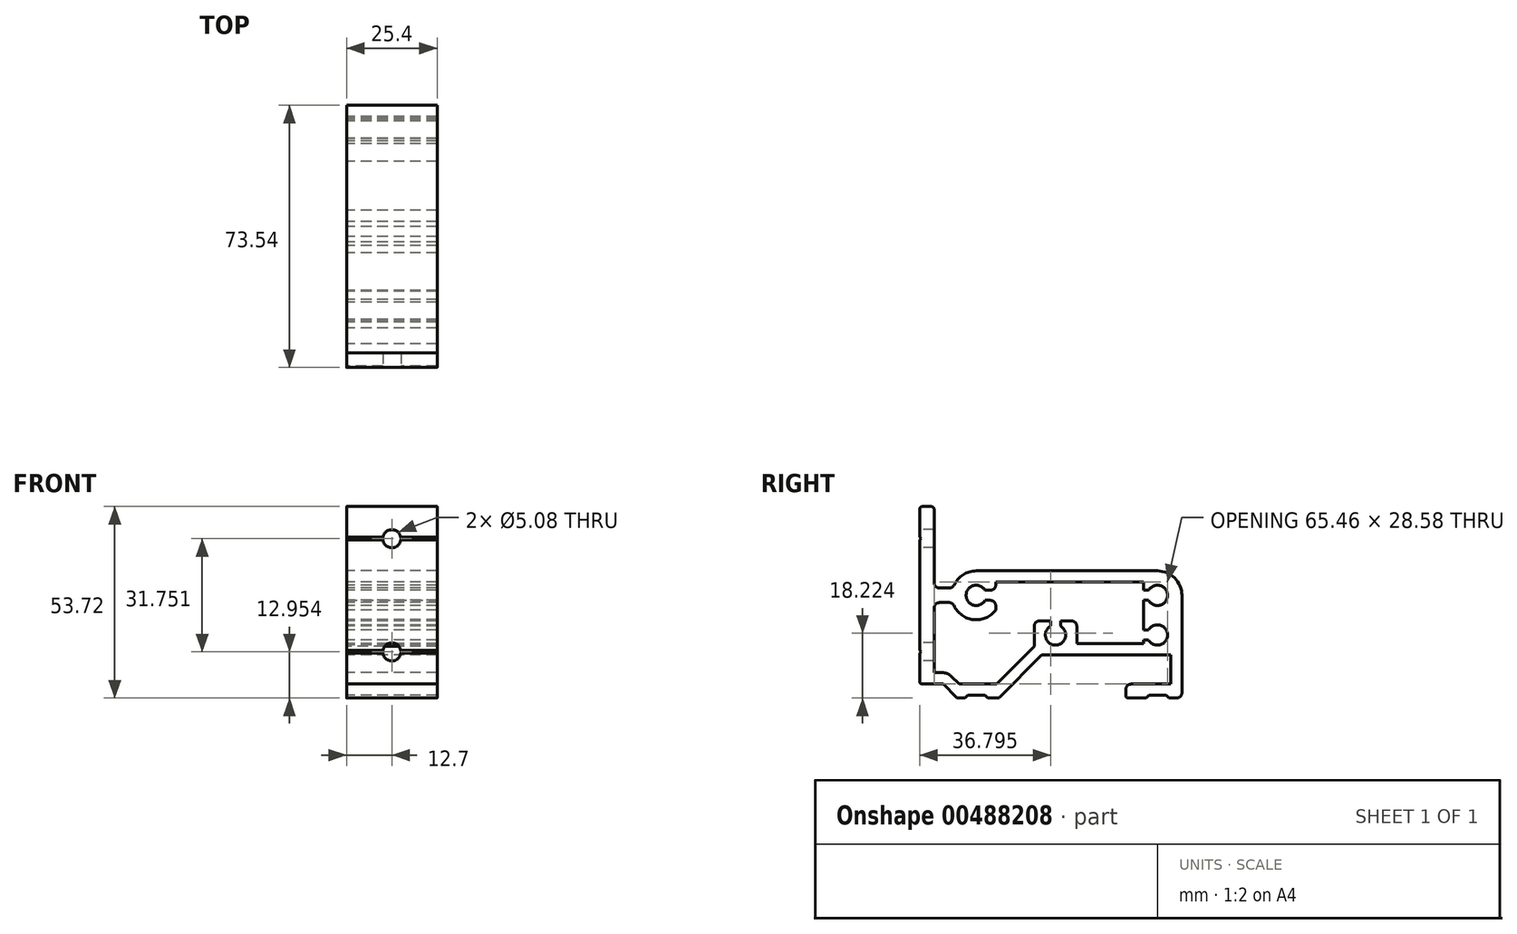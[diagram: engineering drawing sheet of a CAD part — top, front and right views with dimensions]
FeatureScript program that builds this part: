
annotation { "Feature Type Name" : "Feature", "Feature Type Description" : "" }
export const myFeature = defineFeature(function(context is Context, id is Id, definition is map)
    precondition{}
    {
        {
            var Q0;
            Q0=qCreatedBy(makeId("Right.planeOp"),FACE);
            var sketch = newSketch(context, id + "F0", { "sketchPlane" : qUnion([Q0])});
            skLineSegment(sketch, "E0", {"start": v(-16.95, 3.37) * mm, "end": v(-18.41, 3.37) * mm});
            skArc(sketch, "E1", {"start": v(-18.41, 3.37) * mm, "mid": v(-23.74, 1.97) * mm, "end": v(-18.41, 0.57) * mm});
            skLineSegment(sketch, "E2", {"start": v(-18.41, 0.57) * mm, "end": v(-16.95, 0.57) * mm});
            skArc(sketch, "E3", {"start": v(-16.95, 0.57) * mm, "mid": v(-15.88, 0.13) * mm, "end": v(-15.43, -0.95) * mm});
            skLineSegment(sketch, "E4", {"start": v(-15.43, -0.95) * mm, "end": v(-15.43, -2.18) * mm});
            skArc(sketch, "E5", {"start": v(-15.43, -2.18) * mm, "mid": v(-21.62, -4.85) * mm, "end": v(-27.1, -0.94) * mm});
            skArc(sketch, "E6", {"start": v(-27.1, -0.94) * mm, "mid": v(-27.66, -0.3) * mm, "end": v(-28.48, -0.06) * mm});
            skLineSegment(sketch, "E7", {"start": v(-28.48, -0.06) * mm, "end": v(-31.18, -0.06) * mm});
            skArc(sketch, "E8", {"start": v(-31.18, -0.06) * mm, "mid": v(-32.26, -0.5) * mm, "end": v(-32.7, -1.59) * mm});
            skLineSegment(sketch, "E9", {"start": v(-32.7, -1.59) * mm, "end": v(-32.7, -19.75) * mm});
            skLineSegment(sketch, "E10", {"start": v(-32.7, -19.75) * mm, "end": v(-30.16, -19.75) * mm});
            skArc(sketch, "E11", {"start": v(-30.16, -19.75) * mm, "mid": v(-28.95, -20) * mm, "end": v(-27.92, -20.68) * mm});
            skLineSegment(sketch, "E12", {"start": v(-27.92, -20.68) * mm, "end": v(-25.67, -22.92) * mm});
            skLineSegment(sketch, "E13", {"start": v(-25.67, -22.92) * mm, "end": v(-15.18, -22.92) * mm});
            skLineSegment(sketch, "E14", {"start": v(-15.18, -22.92) * mm, "end": v(-4.64, -12.38) * mm});
            skLineSegment(sketch, "E15", {"start": v(-4.64, -12.38) * mm, "end": v(-4.64, -6.73) * mm});
            skArc(sketch, "E16", {"start": v(-4.64, -6.73) * mm, "mid": v(-4.19, -5.65) * mm, "end": v(-3.11, -5.2) * mm});
            skLineSegment(sketch, "E17", {"start": v(-3.11, -5.2) * mm, "end": v(-0.06, -5.2) * mm});
            skLineSegment(sketch, "E18", {"start": v(-0.06, -5.2) * mm, "end": v(-0.06, -6.67) * mm});
            skArc(sketch, "E19", {"start": v(-0.06, -6.67) * mm, "mid": v(1.33, -11.99) * mm, "end": v(2.73, -6.67) * mm});
            skLineSegment(sketch, "E20", {"start": v(2.73, -6.67) * mm, "end": v(2.73, -5.2) * mm});
            skLineSegment(sketch, "E21", {"start": v(2.73, -5.2) * mm, "end": v(5.78, -5.2) * mm});
            skArc(sketch, "E22", {"start": v(5.78, -5.2) * mm, "mid": v(6.86, -5.65) * mm, "end": v(7.3, -6.73) * mm});
            skLineSegment(sketch, "E23", {"start": v(7.3, -6.73) * mm, "end": v(7.3, -11.62) * mm});
            skLineSegment(sketch, "E24", {"start": v(7.3, -11.62) * mm, "end": v(25.97, -11.62) * mm});
            skLineSegment(sketch, "E25", {"start": v(25.97, -11.62) * mm, "end": v(25.97, -10.54) * mm});
            skLineSegment(sketch, "E26", {"start": v(25.97, -10.54) * mm, "end": v(27.43, -10.54) * mm});
            skArc(sketch, "E27", {"start": v(27.43, -10.54) * mm, "mid": v(32.75, -9.14) * mm, "end": v(27.43, -7.75) * mm});
            skLineSegment(sketch, "E28", {"start": v(27.43, -7.75) * mm, "end": v(25.97, -7.75) * mm});
            skLineSegment(sketch, "E29", {"start": v(25.97, -7.75) * mm, "end": v(25.97, 0.57) * mm});
            skLineSegment(sketch, "E30", {"start": v(25.97, 0.57) * mm, "end": v(27.43, 0.57) * mm});
            skArc(sketch, "E31", {"start": v(27.43, 0.57) * mm, "mid": v(32.75, 1.97) * mm, "end": v(27.43, 3.37) * mm});
            skLineSegment(sketch, "E32", {"start": v(27.43, 3.37) * mm, "end": v(25.97, 3.37) * mm});
            skLineSegment(sketch, "E33", {"start": v(25.97, 3.37) * mm, "end": v(25.97, 5.65) * mm});
            skLineSegment(sketch, "E34", {"start": v(25.97, 5.65) * mm, "end": v(-15.43, 5.65) * mm});
            skLineSegment(sketch, "E35", {"start": v(-15.43, 5.65) * mm, "end": v(-15.43, 4.89) * mm});
            skArc(sketch, "E36", {"start": v(-15.43, 4.89) * mm, "mid": v(-15.88, 3.81) * mm, "end": v(-16.95, 3.37) * mm});
            skLineSegment(sketch, "E37", {"start": v(-36.77, 18.22) * mm, "end": v(-36.77, 26.1) * mm});
            skArc(sketch, "E38", {"start": v(-36.77, 26.1) * mm, "mid": v(-36.54, 26.64) * mm, "end": v(-36, 26.86) * mm});
            skLineSegment(sketch, "E39", {"start": v(-36, 26.86) * mm, "end": v(-33.46, 26.86) * mm});
            skArc(sketch, "E40", {"start": v(-33.46, 26.86) * mm, "mid": v(-32.93, 26.64) * mm, "end": v(-32.7, 26.1) * mm});
            skLineSegment(sketch, "E41", {"start": v(-32.7, 26.1) * mm, "end": v(-32.7, 5.52) * mm});
            skArc(sketch, "E42", {"start": v(-32.7, 5.52) * mm, "mid": v(-32.26, 4.45) * mm, "end": v(-31.18, 4) * mm});
            skLineSegment(sketch, "E43", {"start": v(-31.18, 4) * mm, "end": v(-28.48, 4) * mm});
            skArc(sketch, "E44", {"start": v(-28.48, 4) * mm, "mid": v(-27.66, 4.24) * mm, "end": v(-27.1, 4.88) * mm});
            skArc(sketch, "E45", {"start": v(-27.1, 4.88) * mm, "mid": v(-24.57, 7.76) * mm, "end": v(-20.9, 8.83) * mm});
            skLineSegment(sketch, "E46", {"start": v(-20.9, 8.83) * mm, "end": v(29.9, 8.83) * mm});
            skArc(sketch, "E47", {"start": v(29.9, 8.83) * mm, "mid": v(34.76, 6.82) * mm, "end": v(36.77, 1.97) * mm});
            skLineSegment(sketch, "E48", {"start": v(36.77, 1.97) * mm, "end": v(36.77, -25.34) * mm});
            skArc(sketch, "E49", {"start": v(36.77, -25.34) * mm, "mid": v(36.32, -26.41) * mm, "end": v(35.24, -26.86) * mm});
            skLineSegment(sketch, "E50", {"start": v(35.24, -26.86) * mm, "end": v(33.08, -26.86) * mm});
            skLineSegment(sketch, "E51", {"start": v(33.08, -26.86) * mm, "end": v(32.32, -26.1) * mm});
            skLineSegment(sketch, "E52", {"start": v(32.32, -26.1) * mm, "end": v(27.5, -26.1) * mm});
            skLineSegment(sketch, "E53", {"start": v(27.5, -26.1) * mm, "end": v(26.73, -26.86) * mm});
            skLineSegment(sketch, "E54", {"start": v(26.73, -26.86) * mm, "end": v(21.78, -26.86) * mm});
            skArc(sketch, "E55", {"start": v(21.78, -26.86) * mm, "mid": v(21.24, -26.64) * mm, "end": v(21.02, -26.1) * mm});
            skLineSegment(sketch, "E56", {"start": v(21.02, -26.1) * mm, "end": v(21.02, -24.45) * mm});
            skArc(sketch, "E57", {"start": v(21.02, -24.45) * mm, "mid": v(21.46, -23.37) * mm, "end": v(22.54, -22.92) * mm});
            skLineSegment(sketch, "E58", {"start": v(22.54, -22.92) * mm, "end": v(33.6, -22.92) * mm});
            skLineSegment(sketch, "E59", {"start": v(33.6, -22.92) * mm, "end": v(33.6, -14.8) * mm});
            skLineSegment(sketch, "E60", {"start": v(33.6, -14.8) * mm, "end": v(-2.56, -14.8) * mm});
            skLineSegment(sketch, "E61", {"start": v(-2.56, -14.8) * mm, "end": v(-14.4, -26.64) * mm});
            skArc(sketch, "E62", {"start": v(-14.4, -26.64) * mm, "mid": v(-14.65, -26.8) * mm, "end": v(-14.94, -26.86) * mm});
            skLineSegment(sketch, "E63", {"start": v(-14.94, -26.86) * mm, "end": v(-17.72, -26.86) * mm});
            skLineSegment(sketch, "E64", {"start": v(-17.72, -26.86) * mm, "end": v(-18.48, -26.1) * mm});
            skLineSegment(sketch, "E65", {"start": v(-18.48, -26.1) * mm, "end": v(-23.3, -26.1) * mm});
            skLineSegment(sketch, "E66", {"start": v(-23.3, -26.1) * mm, "end": v(-24.07, -26.86) * mm});
            skLineSegment(sketch, "E67", {"start": v(-24.07, -26.86) * mm, "end": v(-25.9, -26.86) * mm});
            skArc(sketch, "E68", {"start": v(-25.9, -26.86) * mm, "mid": v(-26.2, -26.8) * mm, "end": v(-26.45, -26.64) * mm});
            skLineSegment(sketch, "E69", {"start": v(-26.45, -26.64) * mm, "end": v(-30.16, -22.92) * mm});
            skLineSegment(sketch, "E70", {"start": v(-30.16, -22.92) * mm, "end": v(-36, -22.92) * mm});
            skArc(sketch, "E71", {"start": v(-36, -22.92) * mm, "mid": v(-36.54, -22.7) * mm, "end": v(-36.77, -22.16) * mm});
            skLineSegment(sketch, "E72", {"start": v(-36.77, -22.16) * mm, "end": v(-36.77, -14.29) * mm});
            skLineSegment(sketch, "E73", {"start": v(-36.77, -14.29) * mm, "end": v(-36.39, -13.9) * mm});
            skLineSegment(sketch, "E74", {"start": v(-36.39, -13.9) * mm, "end": v(-36.77, -13.53) * mm});
            skLineSegment(sketch, "E75", {"start": v(-36.77, -13.53) * mm, "end": v(-36.77, 17.46) * mm});
            skLineSegment(sketch, "E76", {"start": v(-36.77, 17.46) * mm, "end": v(-36.39, 17.84) * mm});
            skLineSegment(sketch, "E77", {"start": v(-36.39, 17.84) * mm, "end": v(-36.77, 18.22) * mm});
            skSolve(sketch);
        }
        {
            var Q0;
            Q0=makeQuery(id+"F0.imprint","IMPRINT",FACE,{"disambiguationData":[TD([[makeQuery(id+"F0.imprint","IMPRINT",EDGE,{"derivedFrom":sQuery(id+"F0.wireOp",EDGE,"E0")}),-1.0]])]});
            extrude(context, id + "F1", {"entities" : qUnion([Q0]), "depth" : 25.4 * mm});
        }
        {
            var Q0;
            Q0=makeQuery(id+"F1.opExtrude","SWEPT_FACE",FACE,{"disambiguationData":[OSD([sQuery(id+"F0.wireOp",EDGE,"E75")])]});
            var sketch = newSketch(context, id + "F2", { "sketchPlane" : qUnion([Q0])});
            skLineSegment(sketch, "E78", {"start": v(0, 17.46) * mm, "end": v(12.7, 17.46) * mm});
            skLineSegment(sketch, "E79", {"start": v(12.7, 17.46) * mm, "end": v(12.7, 17.84) * mm});
            skCircle(sketch, "E80", {"center": v(12.7, 17.84) * mm, "radius": 2.54 * mm});
            skLineSegment(sketch, "E81", {"start": v(0, -13.53) * mm, "end": v(12.7, -13.53) * mm});
            skLineSegment(sketch, "E82", {"start": v(12.7, -13.53) * mm, "end": v(12.7, -13.9) * mm});
            skCircle(sketch, "E83", {"center": v(12.7, -13.9) * mm, "radius": 2.54 * mm});
            skSolve(sketch);
        }
        {
            var Q0;
            Q0 = qSketchRegion(id + "F2", true);
            extrude(context, id + "F3", {"entities" : qUnion([Q0]), "operationType" : NewBodyOperationType.REMOVE, "oppositeDirection" : true, "depth" : 25.4 * mm, "offsetDistance" : 25.4 * mm});
        }
    });
